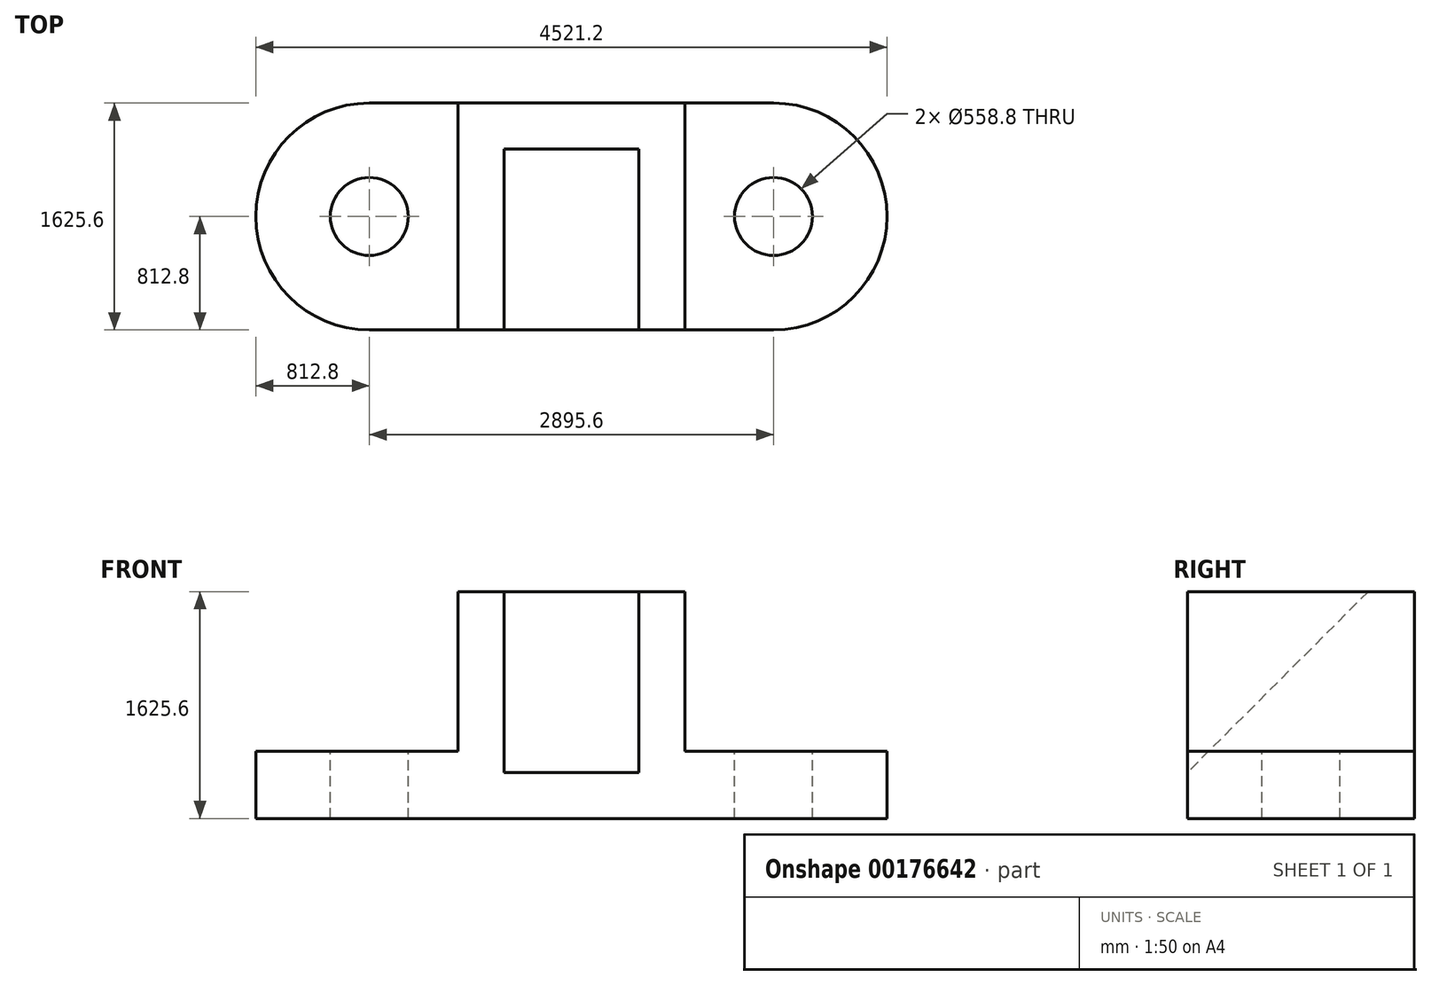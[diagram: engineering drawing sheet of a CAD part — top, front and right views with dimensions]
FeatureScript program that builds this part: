
annotation { "Feature Type Name" : "Feature", "Feature Type Description" : "" }
export const myFeature = defineFeature(function(context is Context, id is Id, definition is map)
    precondition{}
    {
        {
            var Q0;
            Q0=qCreatedBy(makeId("Top.planeOp"),FACE);
            var sketch = newSketch(context, id + "F0", { "sketchPlane" : qUnion([Q0])});
            skLineSegment(sketch, "E0.bottom", {"start": v(-1447.8, 812.8) * mm, "end": v(1447.8, 812.8) * mm});
            skLineSegment(sketch, "E0.top", {"start": v(-1447.8, -812.8) * mm, "end": v(1447.8, -812.8) * mm});
            skLineSegment(sketch, "E0.left", {"start": v(-1447.8, 812.8) * mm, "end": v(-1447.8, -812.8) * mm});
            skLineSegment(sketch, "E0.right", {"start": v(1447.8, 812.8) * mm, "end": v(1447.8, -812.8) * mm});
            skPoint(sketch, "E0.middle", {"position": v(0, 0) * mm});
            skArc(sketch, "E1", {"start": v(-1447.8, 812.8) * mm, "mid": v(-2260.6, 0) * mm, "end": v(-1447.8, -812.8) * mm});
            skArc(sketch, "E2", {"start": v(1447.8, -812.8) * mm, "mid": v(2260.6, 0) * mm, "end": v(1447.8, 812.8) * mm});
            skSolve(sketch);
        }
        {
            var Q0;
            Q0=makeQuery(id+"F0.imprint","IMPRINT",FACE,{"disambiguationData":[TD([[makeQuery(id+"F0.imprint","IMPRINT",EDGE,{"derivedFrom":sQuery(id+"F0.wireOp",EDGE,"E0.bottom")}),-1.0]])]});
            var Q1;
            Q1=makeQuery(id+"F0.imprint","IMPRINT",FACE,{"disambiguationData":[TD([[makeQuery(id+"F0.imprint","IMPRINT",EDGE,{"derivedFrom":sQuery(id+"F0.wireOp",EDGE,"E0.left")}),-1.0]])]});
            var Q2;
            Q2=makeQuery(id+"F0.imprint","IMPRINT",FACE,{"disambiguationData":[TD([[makeQuery(id+"F0.imprint","IMPRINT",EDGE,{"derivedFrom":sQuery(id+"F0.wireOp",EDGE,"E0.right")}),1.0]])]});
            extrude(context, id + "F1", {"entities" : qUnion([Q0, Q1, Q2]), "depth" : 482.6 * mm});
        }
        {
            var Q0;
            Q0=makeQuery(id+"F1.opExtrude","CAP_FACE",FACE,{"disambiguationData":[OSD([sQuery(id+"F0.wireOp",EDGE,"E0.bottom"),sQuery(id+"F0.wireOp",EDGE,"E0.top"),sQuery(id+"F0.wireOp",EDGE,"E1"),sQuery(id+"F0.wireOp",EDGE,"E2")])],"isStart":false});
            var sketch = newSketch(context, id + "F2", { "sketchPlane" : qUnion([Q0])});
            skLineSegment(sketch, "E3.bottom", {"start": v(-812.8, 812.8) * mm, "end": v(812.8, 812.8) * mm});
            skLineSegment(sketch, "E3.top", {"start": v(-812.8, -812.8) * mm, "end": v(812.8, -812.8) * mm});
            skLineSegment(sketch, "E3.left", {"start": v(-812.8, 812.8) * mm, "end": v(-812.8, -812.8) * mm});
            skLineSegment(sketch, "E3.right", {"start": v(812.8, 812.8) * mm, "end": v(812.8, -812.8) * mm});
            skPoint(sketch, "E3.middle", {"position": v(0, 0) * mm});
            skSolve(sketch);
        }
        {
            var Q0;
            Q0 = qSketchRegion(id + "F2", true);
            extrude(context, id + "F3", {"entities" : qUnion([Q0]), "operationType" : NewBodyOperationType.ADD, "depth" : 1143 * mm});
        }
        {
            var Q0;
            Q0=makeQuery(id+"F3.opExtrude","CAP_FACE",FACE,{"disambiguationData":[OSD([sQuery(id+"F2.wireOp",EDGE,"E3.bottom"),sQuery(id+"F2.wireOp",EDGE,"E3.top"),sQuery(id+"F2.wireOp",EDGE,"E3.left"),sQuery(id+"F2.wireOp",EDGE,"E3.right")])],"isStart":false});
            var sketch = newSketch(context, id + "F4", { "sketchPlane" : qUnion([Q0])});
            skLineSegment(sketch, "E4", {"start": v(-812.8, -812.8) * mm, "end": v(-482.6, -812.8) * mm});
            skLineSegment(sketch, "E5", {"start": v(812.8, -812.8) * mm, "end": v(482.6, -812.8) * mm});
            skLineSegment(sketch, "E6.bottom", {"start": v(-482.6, -812.8) * mm, "end": v(482.6, -812.8) * mm});
            skLineSegment(sketch, "E6.top", {"start": v(-482.6, 482.6) * mm, "end": v(482.6, 482.6) * mm});
            skLineSegment(sketch, "E6.left", {"start": v(-482.6, -812.8) * mm, "end": v(-482.6, 482.6) * mm});
            skLineSegment(sketch, "E6.right", {"start": v(482.6, -812.8) * mm, "end": v(482.6, 482.6) * mm});
            skSolve(sketch);
        }
        {
            var Q0;
            Q0=makeQuery(id+"F4.imprint","IMPRINT",FACE,{"disambiguationData":[TD([[makeQuery(id+"F4.imprint","IMPRINT",EDGE,{"derivedFrom":sQuery(id+"F4.wireOp",EDGE,"E6.bottom")}),1.0]])]});
            extrude(context, id + "F5", {"entities" : qUnion([Q0]), "operationType" : NewBodyOperationType.REMOVE, "oppositeDirection" : true, "depth" : 1295.4 * mm});
        }
        {
            var Q0;
            Q0=makeQuery(id+"F5.boolean.opBoolean","COPY",FACE,{"derivedFrom":makeQuery(id+"F5.opExtrude","SWEPT_FACE",FACE,{"disambiguationData":[OSD([sQuery(id+"F4.wireOp",EDGE,"E6.left")])]})});
            var sketch = newSketch(context, id + "F6", { "sketchPlane" : qUnion([Q0])});
            skLineSegment(sketch, "E7", {"start": v(482.6, 1625.6) * mm, "end": v(-812.8, 330.2) * mm});
            skSolve(sketch);
        }
        {
            var Q0;
            Q0 = qSketchRegion(id + "F6", true);
            var Q1;
            Q1=makeQuery(id+"F6.imprint","IMPRINT",FACE,{"disambiguationData":[TD([[makeQuery(id+"F6.imprint","IMPRINT",EDGE,{"derivedFrom":sQuery(id+"F6.wireOp",EDGE,"E7")}),1.0]])]});
            extrude(context, id + "F7", {"entities" : qUnion([Q0, Q1]), "operationType" : NewBodyOperationType.ADD, "depth" : 965.2 * mm});
        }
        {
            var Q0;
            {var subQ0=sQuery(id+"F0.wireOp",EDGE,"E2");var subQ1=sQuery(id+"F0.wireOp",EDGE,"E0.top");var subQ2=sQuery(id+"F0.wireOp",EDGE,"E0.bottom");Q0=makeQuery(id+"F3.boolean.opBoolean","SPLIT",FACE,{"disambiguationData":[TD([makeQuery(id+"F1.opExtrude","SWEPT_FACE",FACE,{"disambiguationData":[OSD([subQ0])]})])],"derivedFrom":makeQuery(id+"F1.opExtrude","CAP_FACE",FACE,{"disambiguationData":[OSD([subQ2,subQ1,sQuery(id+"F0.wireOp",EDGE,"E1"),subQ0])],"isStart":false})});}
            var sketch = newSketch(context, id + "F8", { "sketchPlane" : qUnion([Q0])});
            skPoint(sketch, "E8.endSnap0", {"position": v(812.8, 0) * mm});
            skCircle(sketch, "E9", {"center": v(1447.8, 0) * mm, "radius": 279.4 * mm});
            skSolve(sketch);
        }
        {
            var Q0;
            {var subQ0=sQuery(id+"F0.wireOp",EDGE,"E1");var subQ1=sQuery(id+"F0.wireOp",EDGE,"E0.top");var subQ2=sQuery(id+"F0.wireOp",EDGE,"E0.bottom");Q0=makeQuery(id+"F3.boolean.opBoolean","SPLIT",FACE,{"disambiguationData":[TD([makeQuery(id+"F1.opExtrude","SWEPT_FACE",FACE,{"disambiguationData":[OSD([subQ0])]})])],"derivedFrom":makeQuery(id+"F1.opExtrude","CAP_FACE",FACE,{"disambiguationData":[OSD([subQ2,subQ1,subQ0,sQuery(id+"F0.wireOp",EDGE,"E2")])],"isStart":false})});}
            var sketch = newSketch(context, id + "F9", { "sketchPlane" : qUnion([Q0])});
            skPoint(sketch, "E10.endSnap0", {"position": v(-812.8, 0) * mm});
            skCircle(sketch, "E11", {"center": v(-1447.8, 0) * mm, "radius": 279.4 * mm});
            skSolve(sketch);
        }
        {
            var Q0;
            Q0=makeQuery(id+"F9.imprint","IMPRINT",FACE,{"disambiguationData":[TD([[makeQuery(id+"F9.imprint","IMPRINT",EDGE,{"derivedFrom":sQuery(id+"F9.wireOp",EDGE,"E11")}),1.0]])]});
            extrude(context, id + "F10", {"entities" : qUnion([Q0]), "operationType" : NewBodyOperationType.REMOVE, "oppositeDirection" : true, "depth" : 7620 * mm});
        }
        {
            var Q0;
            Q0=makeQuery(id+"F8.imprint","IMPRINT",FACE,{"disambiguationData":[TD([[makeQuery(id+"F8.imprint","IMPRINT",EDGE,{"derivedFrom":sQuery(id+"F8.wireOp",EDGE,"E9")}),1.0]])]});
            extrude(context, id + "F11", {"entities" : qUnion([Q0]), "operationType" : NewBodyOperationType.ADD, "depth" : 15240 * mm});
        }
        {
            var Q0;
            Q0=makeQuery(id+"F11.opExtrude","CAP_FACE",FACE,{"disambiguationData":[OSD([sQuery(id+"F8.wireOp",EDGE,"E9")])],"isStart":false});
            extrude(context, id + "F12", {"entities" : qUnion([Q0]), "operationType" : NewBodyOperationType.REMOVE, "oppositeDirection" : true, "depth" : 20320 * mm});
        }
    });
